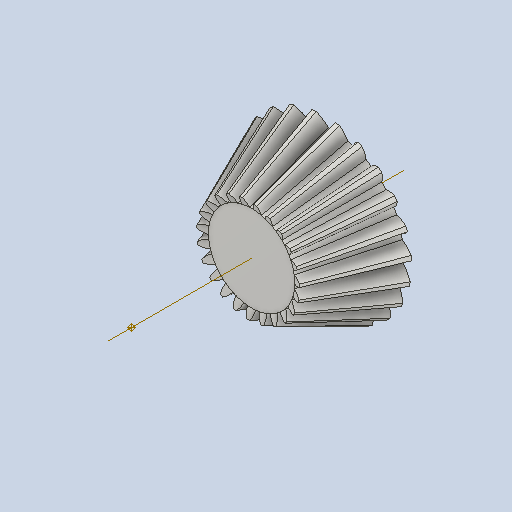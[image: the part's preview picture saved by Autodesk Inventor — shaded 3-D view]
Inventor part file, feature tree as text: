
AUTODESK INVENTOR PART (.ipt)
format: ipt  version: 2023 (Build 270158030, 158C)  size: 577,024 bytes
history: native  units: mm
features: other x24, loft x2, pattern_circular x2, sketch x1
ambient origin geometry x6: Origin, XZ Plane, X Axis, Y Axis, Z Axis, Center Point
bodies: Solid1 (feature_tree)
feature tree (29):
  other  "Top Point"
  other  "Mesh Plane2"
  other  "Teeth Body"
  other  "Start Point"
  other  "Tooth Plane"
  other  "Start Sketch"
  other  "End Point"
  other  "3D Sketch Right"
  other  "End Plane Right"
  loft  "Loft Right"
  pattern_circular  "Circular Pattern Right"  [2 undecoded]
  other  "3D Sketch Left"
  other  "End Plane Left"
  loft  "Loft Left"
  pattern_circular  "Circular Pattern Left"  [2 undecoded]
  other  "Fix Body"
  other  "Mesh Plane"
  other  "Top Plane"
  other  "Teeth Body Sketch"
  other  "End Plane"
  other  "End Sketch"
  other  "Helical Curve Left"
  other  "End Sketch Left"
  other  "Body Sketch"
  sketch  "Sketch6"  dims[d0=69.0mm d1=62.323077mm d2=74.564103mm d3=36.8mm d4=84.377418mm d5=90.0deg d7=13.741113mm d8=14.921461mm d9=31.50969mm d11=37.13mm d12=8.207298mm d15=8.912297mm d16=18.820122mm d17=0.0mm d18=90.0deg d19=0.0mm d20=90.0deg d21=230.0mm d22=360.0deg d26=442.07937mm d27=34.432522mm d28=69.0mm d29=-3.835275mm d30=8.207298mm d31=8.912297mm d32=18.820122mm d35=0.0mm d37=0.0mm d39=0.0mm d40=90.0deg d41=230.0mm d42=360.0deg d46=90.0deg d47=90.0deg d48=0.0mm d49=0.0mm d50=90.0deg d51=1.36591mm d52=0.0mm d53=0.0mm d54=0.0mm d56=20.778221mm d57=42.182765mm d58=32.810765mm d59=25.194941mm d60=19.597228mm d61=25.194941mm d62=19.597228mm d65=442.07937mm d66=31.5mm d67=69.0mm d68=-3.835275mm d69=34.432522mm d70=8.912297mm d71=18.820122mm d72=8.207298mm d73=19.597228mm d74=25.194941mm d75=0.0mm d77=0.0mm d79=0.0mm d80=90.0deg d81=230.0mm d82=360.0deg d84=10.0mm d85=20.0mm d86=20.0mm d87=10.0mm d88=0.0mm d89=0.0mm d90=90.0deg d91=90.0deg d92=90.0deg d93=90.0deg]
  other  "Srf1"
  other  "Helical Curve Right"
  other  "End Sketch Right"
  other  "Pitch Diameter"
note: 4 required parameter values undecoded (feature->parameter linkage not recoverable at this tier; creation-order binding heuristic only, values carry confidence <= 0.55)
